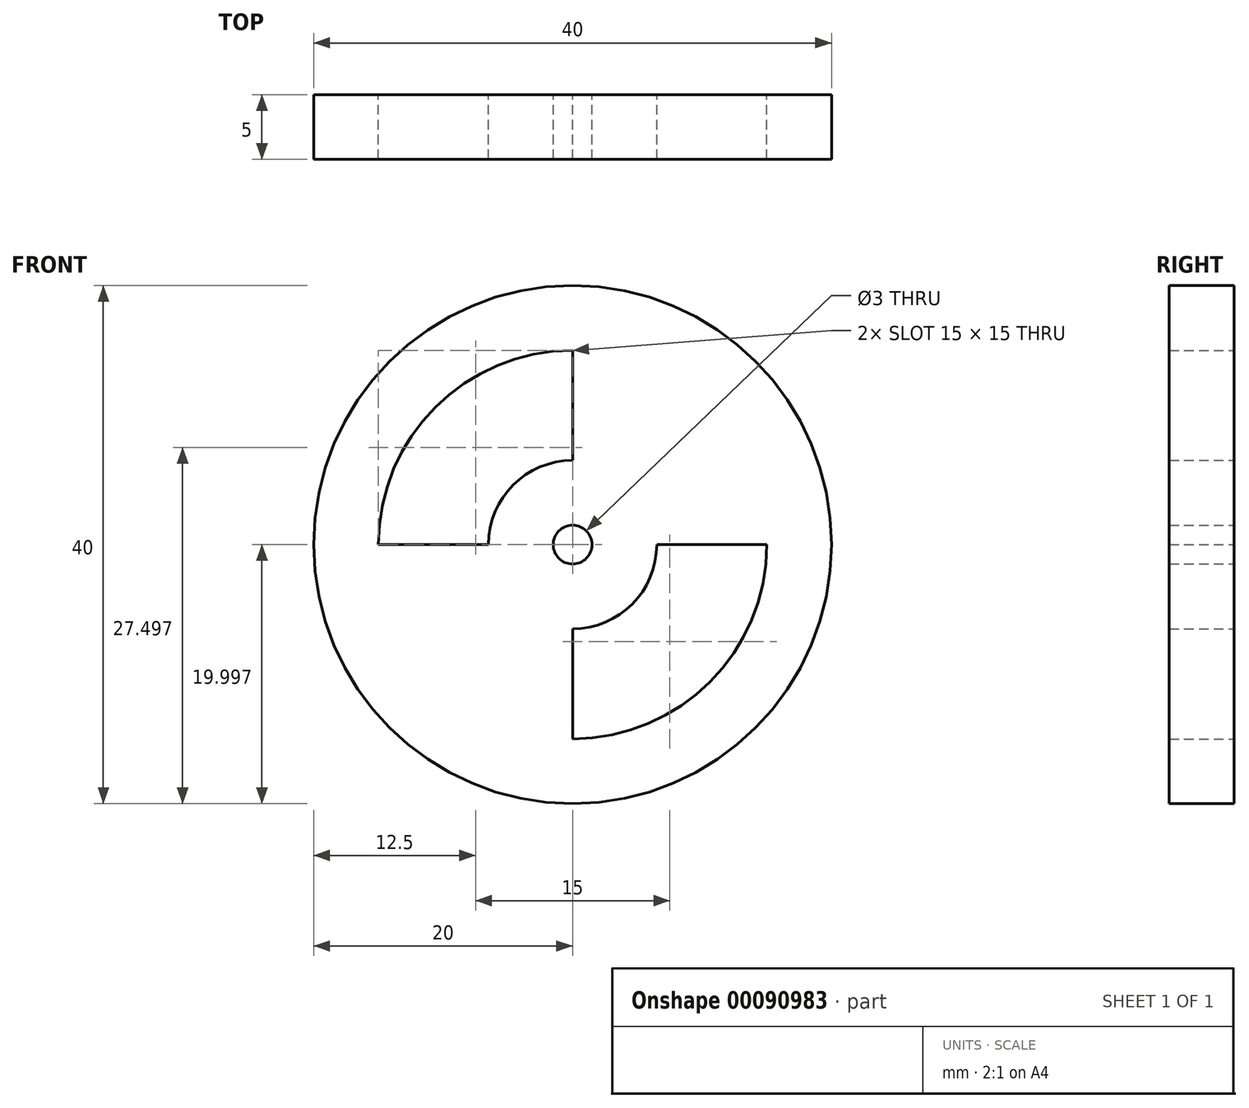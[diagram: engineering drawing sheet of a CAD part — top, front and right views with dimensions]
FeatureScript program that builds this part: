
annotation { "Feature Type Name" : "Feature", "Feature Type Description" : "" }
export const myFeature = defineFeature(function(context is Context, id is Id, definition is map)
    precondition{}
    {
        {
            var Q0;
            Q0=qCreatedBy(makeId("Front.planeOp"),FACE);
            var sketch = newSketch(context, id + "F0", { "sketchPlane" : qUnion([Q0])});
            skCircle(sketch, "E0", {"center": v(-80.07, 25.96) * mm, "radius": 20 * mm});
            skCircle(sketch, "E1", {"center": v(-80.07, 25.96) * mm, "radius": 1.5 * mm});
            skArc(sketch, "E2.0", {"start": v(-80.07, 19.46) * mm, "mid": v(-75.47, 21.36) * mm, "end": v(-73.57, 25.96) * mm});
            skArc(sketch, "E3.0", {"start": v(-80.07, 10.96) * mm, "mid": v(-69.46, 15.35) * mm, "end": v(-65.07, 25.96) * mm});
            skLineSegment(sketch, "E4", {"start": v(-80.07, 32.46) * mm, "end": v(-80.07, 40.96) * mm});
            skLineSegment(sketch, "E5", {"start": v(-73.57, 25.96) * mm, "end": v(-65.07, 25.96) * mm});
            skLineSegment(sketch, "E6", {"start": v(-80.07, 19.46) * mm, "end": v(-80.07, 10.96) * mm});
            skLineSegment(sketch, "E7", {"start": v(-86.57, 25.96) * mm, "end": v(-95.07, 25.96) * mm});
            skArc(sketch, "E8.trimOffspring", {"start": v(-80.07, 32.46) * mm, "mid": v(-84.67, 30.55) * mm, "end": v(-86.57, 25.96) * mm});
            skArc(sketch, "E9.trimOffspring", {"start": v(-80.07, 40.96) * mm, "mid": v(-90.68, 36.56) * mm, "end": v(-95.07, 25.96) * mm});
            skSolve(sketch);
        }
        {
            var Q0;
            Q0=makeQuery(id+"F0.imprint","IMPRINT",FACE,{"disambiguationData":[TD([[makeQuery(id+"F0.imprint","IMPRINT",EDGE,{"derivedFrom":sQuery(id+"F0.wireOp",EDGE,"E0")}),1.0]])]});
            var Q1;
            Q1=sQuery(id+"F0.wireOp",EDGE,"E0");
            extrude(context, id + "F1", {"entities" : qUnion([Q0]), "surfaceEntities" : qUnion([Q1]), "depth" : 5 * mm});
        }
    });
